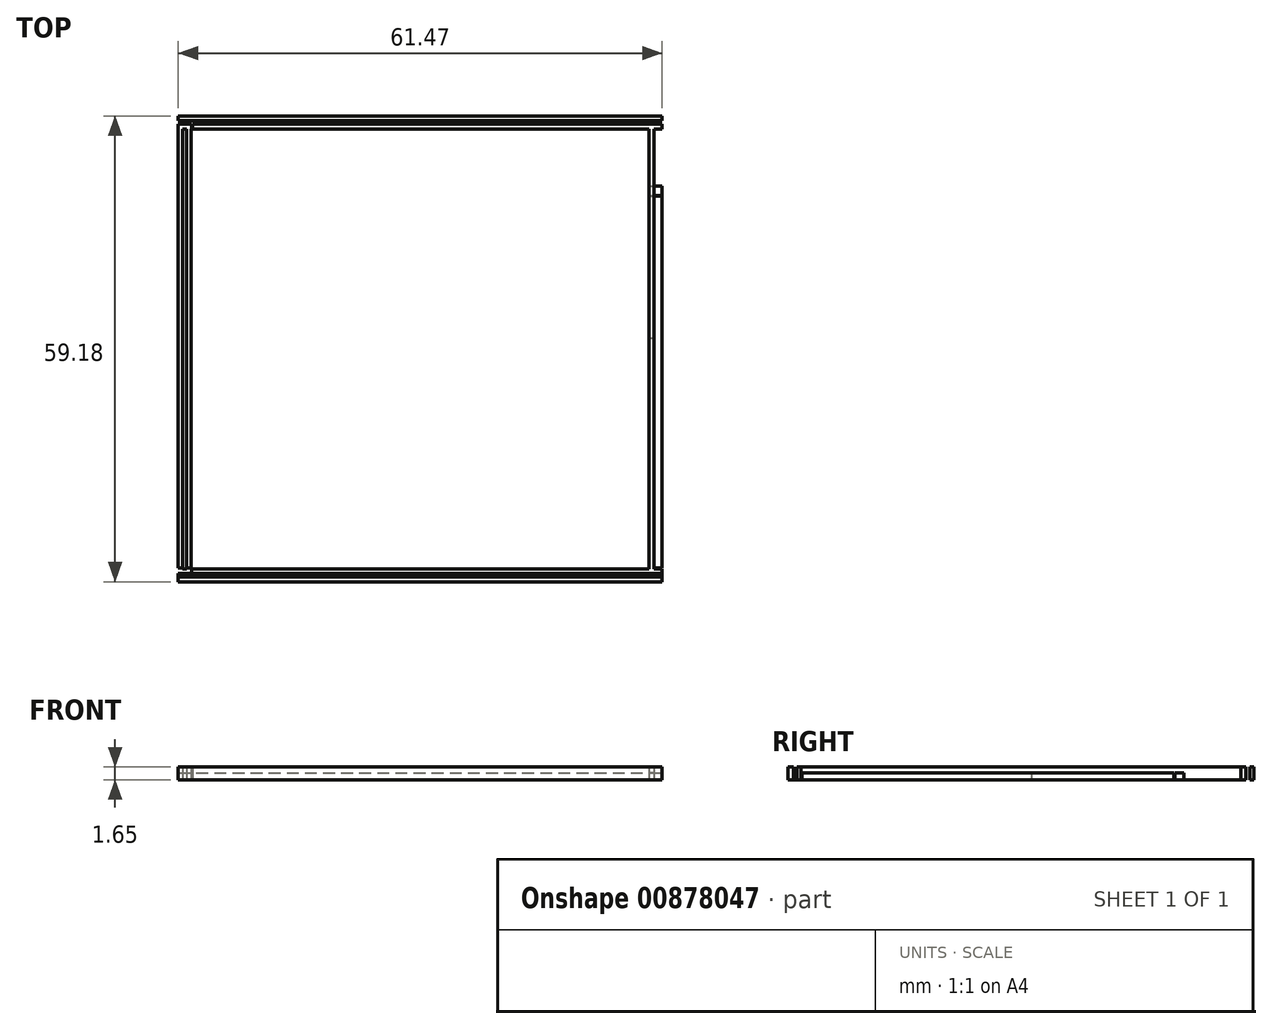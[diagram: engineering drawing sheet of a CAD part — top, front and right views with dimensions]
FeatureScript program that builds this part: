
annotation { "Feature Type Name" : "Feature", "Feature Type Description" : "" }
export const myFeature = defineFeature(function(context is Context, id is Id, definition is map)
    precondition{}
    {
        {
            var Q0;
            Q0=qCreatedBy(makeId("Top.planeOp"),FACE);
            var sketch = newSketch(context, id + "F0", { "sketchPlane" : qUnion([Q0])});
            skLineSegment(sketch, "E0.bottom", {"start": v(0, 0) * mm, "end": v(61.47, 0) * mm});
            skLineSegment(sketch, "E0.top", {"start": v(0, 1.65) * mm, "end": v(61.47, 1.65) * mm});
            skLineSegment(sketch, "E0.left", {"start": v(0, 0) * mm, "end": v(0, 1.65) * mm});
            skLineSegment(sketch, "E0.right", {"start": v(61.47, 0) * mm, "end": v(61.47, 1.65) * mm});
            skLineSegment(sketch, "E1.bottom", {"start": v(0, 1.1) * mm, "end": v(61.47, 1.1) * mm});
            skLineSegment(sketch, "E1.top", {"start": v(0, 0.66) * mm, "end": v(61.47, 0.66) * mm});
            skLineSegment(sketch, "E1.left", {"start": v(0, 1.1) * mm, "end": v(0, 0.66) * mm});
            skLineSegment(sketch, "E1.right", {"start": v(61.47, 1.1) * mm, "end": v(61.47, 0.66) * mm});
            skLineSegment(sketch, "E2.top", {"start": v(0, 59.18) * mm, "end": v(61.47, 59.18) * mm});
            skLineSegment(sketch, "E2.left", {"start": v(0, 0) * mm, "end": v(0, 49) * mm});
            skLineSegment(sketch, "E2.right", {"start": v(61.47, 0) * mm, "end": v(61.47, 59.18) * mm});
            skLineSegment(sketch, "E3.top", {"start": v(0, 57.53) * mm, "end": v(61.47, 57.53) * mm});
            skLineSegment(sketch, "E3.left", {"start": v(0, 59.18) * mm, "end": v(0, 57.53) * mm});
            skLineSegment(sketch, "E3.right", {"start": v(61.47, 59.18) * mm, "end": v(61.47, 57.53) * mm});
            skLineSegment(sketch, "E4.bottom", {"start": v(0, 57.53) * mm, "end": v(1.65, 57.53) * mm});
            skLineSegment(sketch, "E4.top", {"start": v(0, 1.65) * mm, "end": v(1.65, 1.65) * mm});
            skLineSegment(sketch, "E4.left", {"start": v(0, 57.53) * mm, "end": v(0, 1.65) * mm});
            skLineSegment(sketch, "E4.right", {"start": v(1.65, 57.53) * mm, "end": v(1.65, 49.12) * mm});
            skLineSegment(sketch, "E5.bottom", {"start": v(61.47, 57.53) * mm, "end": v(59.82, 57.53) * mm});
            skLineSegment(sketch, "E5.top", {"start": v(61.47, 1.65) * mm, "end": v(59.82, 1.65) * mm});
            skLineSegment(sketch, "E5.left", {"start": v(61.47, 57.53) * mm, "end": v(61.47, 1.65) * mm});
            skLineSegment(sketch, "E5.right", {"start": v(59.82, 57.53) * mm, "end": v(59.82, 1.65) * mm});
            skLineSegment(sketch, "E6.right", {"start": v(61.47, 50.29) * mm, "end": v(61.47, 49.82) * mm});
            skLineSegment(sketch, "E7.bottom", {"start": v(0.58, 57.53) * mm, "end": v(1.05, 57.53) * mm});
            skLineSegment(sketch, "E7.top", {"start": v(0.58, 1.65) * mm, "end": v(1.05, 1.65) * mm});
            skLineSegment(sketch, "E7.left", {"start": v(0.58, 57.53) * mm, "end": v(0.58, 1.65) * mm});
            skLineSegment(sketch, "E7.right", {"start": v(1.05, 57.53) * mm, "end": v(1.05, 1.65) * mm});
            skLineSegment(sketch, "E8.bottom", {"start": v(60.4, 57.53) * mm, "end": v(61.47, 57.53) * mm});
            skLineSegment(sketch, "E8.left", {"start": v(60.4, 57.53) * mm, "end": v(60.4, -1.65) * mm});
            skLineSegment(sketch, "E9.bottom", {"start": v(59.82, 49.1) * mm, "end": v(61.47, 49.1) * mm});
            skLineSegment(sketch, "E9.top", {"start": v(59.82, 49) * mm, "end": v(61.47, 49) * mm});
            skLineSegment(sketch, "E9.left", {"start": v(59.82, 49.1) * mm, "end": v(59.82, 49) * mm});
            skLineSegment(sketch, "E9.right", {"start": v(61.47, 49.1) * mm, "end": v(61.47, 49) * mm});
            skLineSegment(sketch, "E10.bottom", {"start": v(74.5, 57.53) * mm, "end": v(74.4, 57.53) * mm});
            skLineSegment(sketch, "E10.top", {"start": v(74.5, 59.18) * mm, "end": v(74.4, 59.18) * mm});
            skLineSegment(sketch, "E11.bottom", {"start": v(59.82, 1.68) * mm, "end": v(61.47, 1.68) * mm});
            skLineSegment(sketch, "E11.top", {"start": v(59.82, 1.79) * mm, "end": v(61.47, 1.79) * mm});
            skLineSegment(sketch, "E11.left", {"start": v(59.82, 1.68) * mm, "end": v(59.82, 1.79) * mm});
            skLineSegment(sketch, "E11.right", {"start": v(61.47, 1.68) * mm, "end": v(61.47, 1.79) * mm});
            skLineSegment(sketch, "E12.bottom", {"start": v(74.52, 1.65) * mm, "end": v(74.43, 1.65) * mm});
            skLineSegment(sketch, "E12.top", {"start": v(74.52, 0) * mm, "end": v(74.43, 0) * mm});
            skLineSegment(sketch, "E13.bottom", {"start": v(0, 1.69) * mm, "end": v(1.65, 1.69) * mm});
            skLineSegment(sketch, "E13.top", {"start": v(0, 1.8) * mm, "end": v(1.65, 1.8) * mm});
            skLineSegment(sketch, "E13.left", {"start": v(0, 1.69) * mm, "end": v(0, 1.8) * mm});
            skLineSegment(sketch, "E13.right", {"start": v(1.65, 1.69) * mm, "end": v(1.65, 1.8) * mm});
            skLineSegment(sketch, "E14.bottom", {"start": v(1.68, 1.65) * mm, "end": v(1.8, 1.65) * mm});
            skLineSegment(sketch, "E14.top", {"start": v(1.68, 0) * mm, "end": v(1.8, 0) * mm});
            skLineSegment(sketch, "E14.left", {"start": v(1.68, 1.65) * mm, "end": v(1.68, 0) * mm});
            skLineSegment(sketch, "E14.right", {"start": v(1.8, 1.65) * mm, "end": v(1.8, 0) * mm});
            skLineSegment(sketch, "E15.bottom", {"start": v(1.67, 57.53) * mm, "end": v(1.8, 57.53) * mm});
            skLineSegment(sketch, "E15.top", {"start": v(1.67, 59.18) * mm, "end": v(1.8, 59.18) * mm});
            skLineSegment(sketch, "E15.left", {"start": v(1.67, 57.53) * mm, "end": v(1.67, 59.18) * mm});
            skLineSegment(sketch, "E15.right", {"start": v(1.8, 57.53) * mm, "end": v(1.8, 59.18) * mm});
            skLineSegment(sketch, "E16.left", {"start": v(0, 49.12) * mm, "end": v(0, 49) * mm});
            skLineSegment(sketch, "E16.right", {"start": v(1.65, 49.12) * mm, "end": v(1.65, 49) * mm});
            skLineSegment(sketch, "E17", {"start": v(60.4, 30.9) * mm, "end": v(59.82, 30.9) * mm});
            skLineSegment(sketch, "E18.trimOffspring", {"start": v(59.82, 49.82) * mm, "end": v(61.47, 49.82) * mm});
            skLineSegment(sketch, "E19.trimOffspring", {"start": v(59.82, 50.29) * mm, "end": v(61.47, 50.29) * mm});
            skLineSegment(sketch, "E20.bottom", {"start": v(60.4, 57.53) * mm, "end": v(60.85, 57.53) * mm});
            skLineSegment(sketch, "E20.top", {"start": v(60.4, 1.65) * mm, "end": v(60.85, 1.65) * mm});
            skLineSegment(sketch, "E20.left", {"start": v(60.4, 57.53) * mm, "end": v(60.4, 1.65) * mm});
            skLineSegment(sketch, "E20.right", {"start": v(60.85, 57.53) * mm, "end": v(60.85, 1.65) * mm});
            skLineSegment(sketch, "E21.bottom", {"start": v(61.47, 58.63) * mm, "end": v(0, 58.63) * mm});
            skLineSegment(sketch, "E21.top", {"start": v(61.47, 58.13) * mm, "end": v(0, 58.13) * mm});
            skLineSegment(sketch, "E21.left", {"start": v(61.47, 58.63) * mm, "end": v(61.47, 58.13) * mm});
            skLineSegment(sketch, "E21.right", {"start": v(0, 58.63) * mm, "end": v(0, 58.13) * mm});
            skLineSegment(sketch, "E22.trimOffspring", {"start": v(1.65, 49) * mm, "end": v(1.65, 1.65) * mm});
            skLineSegment(sketch, "E23.trimOffspring", {"start": v(0, 49.12) * mm, "end": v(0, 59.18) * mm});
            skLineSegment(sketch, "E24.trimOffspring", {"start": v(74.4, 57.53) * mm, "end": v(74.5, 57.53) * mm});
            skSolve(sketch);
        }
        {
            var Q0;
            {var subQ0=sQuery(id+"F0.wireOp",EDGE,"E1.top");Q0=makeQuery(id+"F0.imprint","IMPRINT",FACE,{"disambiguationData":[TD([[makeQuery(id+"F0.imprint","IMPRINT",EDGE,{"derivedFrom":subQ0}),-1.0]])]});}
            var Q1;
            {var subQ0=sQuery(id+"F0.wireOp",EDGE,"E2.top");Q1=makeQuery(id+"F0.imprint","IMPRINT",FACE,{"disambiguationData":[TD([[makeQuery(id+"F0.imprint","IMPRINT",EDGE,{"derivedFrom":subQ0}),-1.0]])]});}
            var Q2;
            {var subQ0=sQuery(id+"F0.wireOp",EDGE,"E4.left");Q2=makeQuery(id+"F0.imprint","IMPRINT",FACE,{"disambiguationData":[TD([[makeQuery(id+"F0.imprint","IMPRINT",EDGE,{"derivedFrom":subQ0}),1.0]])]});}
            var Q3;
            {var subQ0=sQuery(id+"F0.wireOp",EDGE,"E5.left");Q3=makeQuery(id+"F0.imprint","IMPRINT",FACE,{"disambiguationData":[TD([[makeQuery(id+"F0.imprint","IMPRINT",EDGE,{"derivedFrom":subQ0}),-1.0]])]});}
            var Q4;
            {var subQ8=sQuery(id+"F0.wireOp",EDGE,"E3.top");Q4=makeQuery(id+"F0.imprint","IMPRINT",FACE,{"disambiguationData":[TD([[makeQuery(id+"F0.imprint","IMPRINT",EDGE,{"derivedFrom":subQ8}),1.0]])]});}
            var Q5;
            {var subQ0=sQuery(id+"F0.wireOp",EDGE,"E4.right");Q5=makeQuery(id+"F0.imprint","IMPRINT",FACE,{"disambiguationData":[TD([[makeQuery(id+"F0.imprint","IMPRINT",EDGE,{"derivedFrom":subQ0}),-1.0]])]});}
            var Q6;
            {var subQ0=sQuery(id+"F0.wireOp",EDGE,"E5.right");Q6=makeQuery(id+"F0.imprint","IMPRINT",FACE,{"disambiguationData":[TD([[makeQuery(id+"F0.imprint","IMPRINT",EDGE,{"derivedFrom":subQ0}),1.0]])]});}
            var Q7;
            {var subQ0=sQuery(id+"F0.wireOp",EDGE,"E2.left");var subQ1=sQuery(id+"F0.wireOp",EDGE,"E1.bottom");var subQ2=makeQuery(id+"F0.imprint","INTERSECT",VERTEX,{"derivedFrom":[subQ1,subQ0]});Q7=makeQuery(id+"F0.imprint","IMPRINT",FACE,{"disambiguationData":[TD([[makeQuery(id+"F0.imprint","IMPRINT",EDGE,{"disambiguationData":[TD([[subQ2,-1.0]])],"derivedFrom":subQ1}),1.0]])]});}
            var Q8;
            {var subQ0=sQuery(id+"F0.wireOp",EDGE,"E7.left");var subQ1=sQuery(id+"F0.wireOp",EDGE,"E1.bottom");var subQ2=makeQuery(id+"F0.imprint","INTERSECT",VERTEX,{"derivedFrom":[subQ1,subQ0]});Q8=makeQuery(id+"F0.imprint","IMPRINT",FACE,{"disambiguationData":[TD([[makeQuery(id+"F0.imprint","IMPRINT",EDGE,{"disambiguationData":[TD([[subQ2,-1.0]])],"derivedFrom":subQ1}),1.0]])]});}
            var Q9;
            {var subQ3=sQuery(id+"F0.wireOp",EDGE,"E14.right");var subQ5=sQuery(id+"F0.wireOp",EDGE,"E1.bottom");var subQ6=makeQuery(id+"F0.imprint","INTERSECT",VERTEX,{"derivedFrom":[subQ5,subQ3]});Q9=makeQuery(id+"F0.imprint","IMPRINT",FACE,{"disambiguationData":[TD([[makeQuery(id+"F0.imprint","IMPRINT",EDGE,{"disambiguationData":[TD([[subQ6,-1.0]])],"derivedFrom":subQ5}),1.0]])]});}
            var Q10;
            {var subQ0=sQuery(id+"F0.wireOp",EDGE,"E7.right");var subQ1=sQuery(id+"F0.wireOp",EDGE,"E1.bottom");var subQ2=makeQuery(id+"F0.imprint","INTERSECT",VERTEX,{"derivedFrom":[subQ1,subQ0]});Q10=makeQuery(id+"F0.imprint","IMPRINT",FACE,{"disambiguationData":[TD([[makeQuery(id+"F0.imprint","IMPRINT",EDGE,{"disambiguationData":[TD([[subQ2,-1.0]])],"derivedFrom":subQ1}),1.0]])]});}
            var Q11;
            {var subQ5=sQuery(id+"F0.wireOp",EDGE,"E14.bottom");Q11=makeQuery(id+"F0.imprint","IMPRINT",FACE,{"disambiguationData":[TD([[makeQuery(id+"F0.imprint","IMPRINT",EDGE,{"derivedFrom":subQ5}),-1.0]])]});}
            var Q12;
            {var subQ5=sQuery(id+"F0.wireOp",EDGE,"E12.bottom");Q12=makeQuery(id+"F0.imprint","IMPRINT",FACE,{"disambiguationData":[TD([[makeQuery(id+"F0.imprint","IMPRINT",EDGE,{"derivedFrom":subQ5}),1.0]])]});}
            var Q13;
            {var subQ1=sQuery(id+"F0.wireOp",EDGE,"E1.bottom");var subQ7=sQuery(id+"F0.wireOp",EDGE,"E12.left");var subQ8=makeQuery(id+"F0.imprint","INTERSECT",VERTEX,{"derivedFrom":[subQ1,subQ7]});Q13=makeQuery(id+"F0.imprint","IMPRINT",FACE,{"disambiguationData":[TD([[makeQuery(id+"F0.imprint","IMPRINT",EDGE,{"disambiguationData":[TD([[subQ8,-1.0]])],"derivedFrom":subQ1}),1.0]])]});}
            var Q14;
            {var subQ0=sQuery(id+"F0.wireOp",EDGE,"E8.left");var subQ1=sQuery(id+"F0.wireOp",EDGE,"E1.bottom");var subQ2=makeQuery(id+"F0.imprint","INTERSECT",VERTEX,{"derivedFrom":[subQ1,subQ0]});Q14=makeQuery(id+"F0.imprint","IMPRINT",FACE,{"disambiguationData":[TD([[makeQuery(id+"F0.imprint","IMPRINT",EDGE,{"disambiguationData":[TD([[subQ2,-1.0]])],"derivedFrom":subQ1}),1.0]])]});}
            var Q15;
            {var subQ5=sQuery(id+"F0.wireOp",EDGE,"E11.left");Q15=makeQuery(id+"F0.imprint","IMPRINT",FACE,{"disambiguationData":[TD([[makeQuery(id+"F0.imprint","IMPRINT",EDGE,{"derivedFrom":subQ5}),-1.0]])]});}
            var Q16;
            {var subQ5=sQuery(id+"F0.wireOp",EDGE,"E11.right");Q16=makeQuery(id+"F0.imprint","IMPRINT",FACE,{"disambiguationData":[TD([[makeQuery(id+"F0.imprint","IMPRINT",EDGE,{"derivedFrom":subQ5}),1.0]])]});}
            var Q17;
            {var subQ0=sQuery(id+"F0.wireOp",EDGE,"E2.right");var subQ1=sQuery(id+"F0.wireOp",EDGE,"E1.bottom");var subQ2=makeQuery(id+"F0.imprint","INTERSECT",VERTEX,{"derivedFrom":[subQ1,subQ0]});Q17=makeQuery(id+"F0.imprint","IMPRINT",FACE,{"disambiguationData":[TD([[makeQuery(id+"F0.imprint","IMPRINT",EDGE,{"disambiguationData":[TD([[subQ2,1.0]])],"derivedFrom":subQ1}),1.0]])]});}
            var Q18;
            {var subQ5=sQuery(id+"F0.wireOp",EDGE,"E10.top");Q18=makeQuery(id+"F0.imprint","IMPRINT",FACE,{"disambiguationData":[TD([[makeQuery(id+"F0.imprint","IMPRINT",EDGE,{"derivedFrom":subQ5}),1.0]])]});}
            var Q19;
            {var subQ3=sQuery(id+"F0.wireOp",EDGE,"E8.bottom");Q19=makeQuery(id+"F0.imprint","IMPRINT",FACE,{"disambiguationData":[TD([[makeQuery(id+"F0.imprint","IMPRINT",EDGE,{"derivedFrom":subQ3}),1.0]])]});}
            var Q20;
            {var subQ5=sQuery(id+"F0.wireOp",EDGE,"E10.bottom");Q20=makeQuery(id+"F0.imprint","IMPRINT",FACE,{"disambiguationData":[TD([[makeQuery(id+"F0.imprint","IMPRINT",EDGE,{"derivedFrom":subQ5}),-1.0]])]});}
            var Q21;
            {var subQ5=sQuery(id+"F0.wireOp",EDGE,"E9.left");Q21=makeQuery(id+"F0.imprint","IMPRINT",FACE,{"disambiguationData":[TD([[makeQuery(id+"F0.imprint","IMPRINT",EDGE,{"derivedFrom":subQ5}),1.0]])]});}
            var Q22;
            {var subQ5=sQuery(id+"F0.wireOp",EDGE,"E9.right");Q22=makeQuery(id+"F0.imprint","IMPRINT",FACE,{"disambiguationData":[TD([[makeQuery(id+"F0.imprint","IMPRINT",EDGE,{"derivedFrom":subQ5}),-1.0]])]});}
            var Q23;
            {var subQ3=sQuery(id+"F0.wireOp",EDGE,"E7.bottom");Q23=makeQuery(id+"F0.imprint","IMPRINT",FACE,{"disambiguationData":[TD([[makeQuery(id+"F0.imprint","IMPRINT",EDGE,{"derivedFrom":subQ3}),1.0]])]});}
            var Q24;
            {var subQ5=sQuery(id+"F0.wireOp",EDGE,"E15.bottom");Q24=makeQuery(id+"F0.imprint","IMPRINT",FACE,{"disambiguationData":[TD([[makeQuery(id+"F0.imprint","IMPRINT",EDGE,{"derivedFrom":subQ5}),1.0]])]});}
            var Q25;
            {var subQ5=sQuery(id+"F0.wireOp",EDGE,"E15.top");Q25=makeQuery(id+"F0.imprint","IMPRINT",FACE,{"disambiguationData":[TD([[makeQuery(id+"F0.imprint","IMPRINT",EDGE,{"derivedFrom":subQ5}),-1.0]])]});}
            var Q26;
            {var subQ5=sQuery(id+"F0.wireOp",EDGE,"E16.right");Q26=makeQuery(id+"F0.imprint","IMPRINT",FACE,{"disambiguationData":[TD([[makeQuery(id+"F0.imprint","IMPRINT",EDGE,{"derivedFrom":subQ5}),-1.0]])]});}
            var Q27;
            {var subQ5=sQuery(id+"F0.wireOp",EDGE,"E16.left");Q27=makeQuery(id+"F0.imprint","IMPRINT",FACE,{"disambiguationData":[TD([[makeQuery(id+"F0.imprint","IMPRINT",EDGE,{"derivedFrom":subQ5}),1.0]])]});}
            var Q28;
            {var subQ0=sQuery(id+"F0.wireOp",EDGE,"E6.right");Q28=makeQuery(id+"F0.imprint","IMPRINT",FACE,{"disambiguationData":[TD([[makeQuery(id+"F0.imprint","IMPRINT",EDGE,{"derivedFrom":subQ0}),-1.0]])]});}
            extrude(context, id + "F1", {"entities" : qUnion([Q0, Q1, Q2, Q3, Q4, Q5, Q6, Q7, Q8, Q9, Q10, Q11, Q12, Q13, Q14, Q15, Q16, Q17, Q18, Q19, Q20, Q21, Q22, Q23, Q24, Q25, Q26, Q27, Q28]), "depth" : 1.65 * mm, "offsetDistance" : 25.4 * mm});
        }
        {
            var Q0;
            {var subQ0=sQuery(id+"F0.wireOp",EDGE,"E1.bottom");Q0=makeQuery(id+"F0.imprint","IMPRINT",FACE,{"disambiguationData":[TD([[makeQuery(id+"F0.imprint","IMPRINT",EDGE,{"derivedFrom":subQ0}),-1.0]])]});}
            var Q1;
            Q1=makeQuery(id+"F0.imprint","IMPRINT",FACE,{"disambiguationData":[TD([[makeQuery(id+"F0.imprint","IMPRINT",EDGE,{"derivedFrom":sQuery(id+"F0.wireOp",EDGE,"E6.bottom")}),-1.0]])]});
            var Q2;
            Q2=makeQuery(id+"F0.imprint","IMPRINT",FACE,{"disambiguationData":[TD([[makeQuery(id+"F0.imprint","IMPRINT",EDGE,{"derivedFrom":sQuery(id+"F0.wireOp",EDGE,"E7.bottom")}),-1.0]])]});
            var Q3;
            Q3=makeQuery(id+"F0.imprint","IMPRINT",FACE,{"disambiguationData":[TD([[makeQuery(id+"F0.imprint","IMPRINT",EDGE,{"derivedFrom":sQuery(id+"F0.wireOp",EDGE,"E8.bottom")}),-1.0]])]});
            var Q4;
            {var subQ0=sQuery(id+"F0.wireOp",EDGE,"E16.top");var subQ1=sQuery(id+"F0.wireOp",EDGE,"E7.left");var subQ2=makeQuery(id+"F0.imprint","INTERSECT",VERTEX,{"derivedFrom":[subQ1,subQ0]});Q4=makeQuery(id+"F0.imprint","IMPRINT",FACE,{"disambiguationData":[TD([[makeQuery(id+"F0.imprint","IMPRINT",EDGE,{"disambiguationData":[TD([[subQ2,-1.0]])],"derivedFrom":subQ1}),1.0]])]});}
            var Q5;
            {var subQ0=sQuery(id+"F0.wireOp",EDGE,"E9.top");var subQ1=sQuery(id+"F0.wireOp",EDGE,"E8.left");var subQ2=makeQuery(id+"F0.imprint","INTERSECT",VERTEX,{"derivedFrom":[subQ1,subQ0]});Q5=makeQuery(id+"F0.imprint","IMPRINT",FACE,{"disambiguationData":[TD([[makeQuery(id+"F0.imprint","IMPRINT",EDGE,{"disambiguationData":[TD([[subQ2,-1.0]])],"derivedFrom":subQ1}),1.0]])]});}
            var Q6;
            {var subQ5=sQuery(id+"F0.wireOp",EDGE,"E21.left");Q6=makeQuery(id+"F0.imprint","IMPRINT",FACE,{"disambiguationData":[TD([[makeQuery(id+"F0.imprint","IMPRINT",EDGE,{"derivedFrom":subQ5}),-1.0]])]});}
            var Q7;
            {var subQ5=sQuery(id+"F0.wireOp",EDGE,"E20.bottom");Q7=makeQuery(id+"F0.imprint","IMPRINT",FACE,{"disambiguationData":[TD([[makeQuery(id+"F0.imprint","IMPRINT",EDGE,{"derivedFrom":subQ5}),-1.0]])]});}
            var Q8;
            {var subQ0=sQuery(id+"F0.wireOp",EDGE,"E20.left");var subQ1=sQuery(id+"F0.wireOp",EDGE,"E18.trimOffspring");var subQ2=makeQuery(id+"F0.imprint","INTERSECT",VERTEX,{"derivedFrom":[subQ1,subQ0]});Q8=makeQuery(id+"F0.imprint","IMPRINT",FACE,{"disambiguationData":[TD([[makeQuery(id+"F0.imprint","IMPRINT",EDGE,{"disambiguationData":[TD([[subQ2,-1.0]])],"derivedFrom":subQ1}),1.0]])]});}
            var Q9;
            {var subQ0=sQuery(id+"F0.wireOp",EDGE,"E20.left");var subQ1=sQuery(id+"F0.wireOp",EDGE,"E9.bottom");var subQ2=makeQuery(id+"F0.imprint","INTERSECT",VERTEX,{"derivedFrom":[subQ1,subQ0]});Q9=makeQuery(id+"F0.imprint","IMPRINT",FACE,{"disambiguationData":[TD([[makeQuery(id+"F0.imprint","IMPRINT",EDGE,{"disambiguationData":[TD([[subQ2,-1.0]])],"derivedFrom":subQ1}),1.0]])]});}
            var Q10;
            {var subQ0=sQuery(id+"F0.wireOp",EDGE,"E20.left");var subQ4=sQuery(id+"F0.wireOp",EDGE,"E9.top");var subQ5=makeQuery(id+"F0.imprint","INTERSECT",VERTEX,{"derivedFrom":[subQ4,subQ0]});Q10=makeQuery(id+"F0.imprint","IMPRINT",FACE,{"disambiguationData":[TD([[makeQuery(id+"F0.imprint","IMPRINT",EDGE,{"disambiguationData":[TD([[subQ5,-1.0]])],"derivedFrom":subQ4}),-1.0]])]});}
            extrude(context, id + "F2", {"entities" : qUnion([Q0, Q1, Q2, Q3, Q4, Q5, Q6, Q7, Q8, Q9, Q10]), "depth" : 0.89 * mm, "offsetDistance" : 25.4 * mm});
        }
    });
